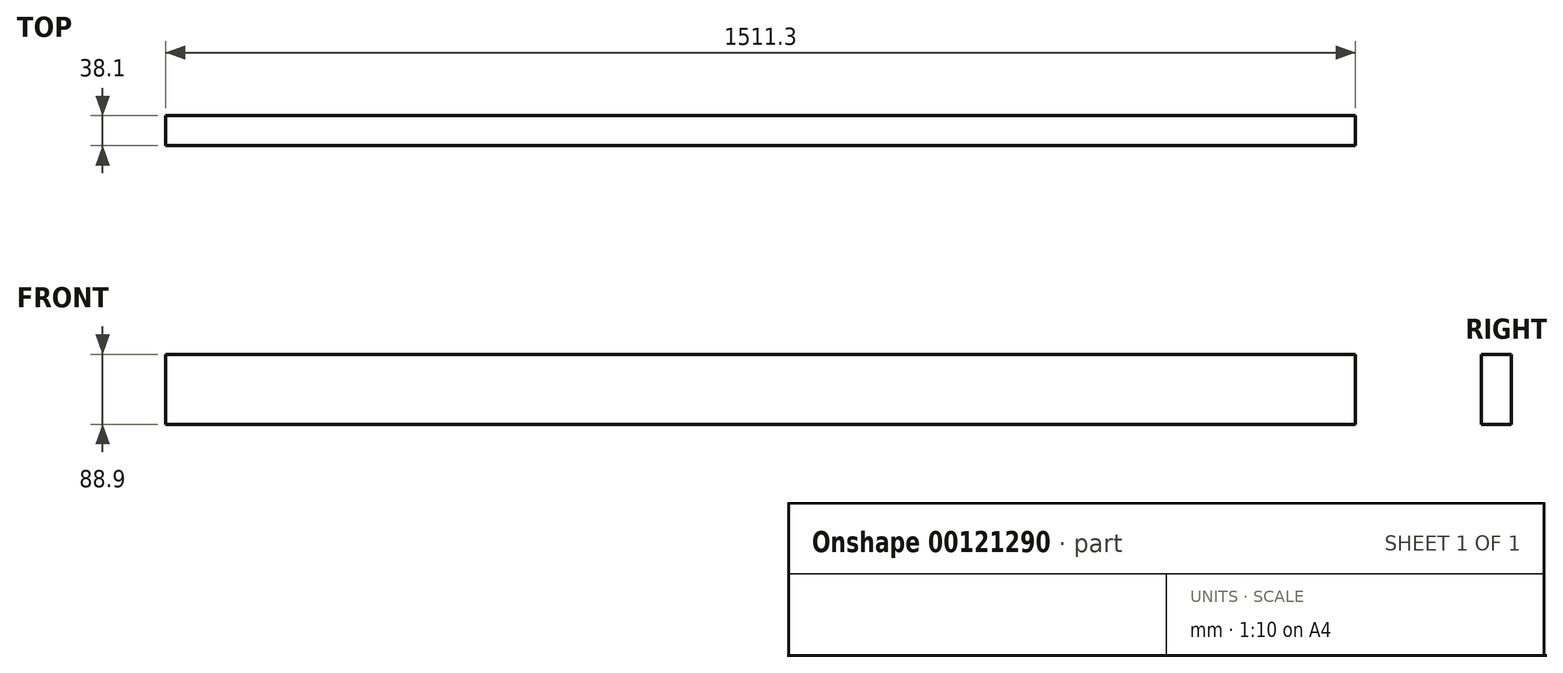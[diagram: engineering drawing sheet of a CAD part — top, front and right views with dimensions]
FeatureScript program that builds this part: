
annotation { "Feature Type Name" : "Feature", "Feature Type Description" : "" }
export const myFeature = defineFeature(function(context is Context, id is Id, definition is map)
    precondition{}
    {
        {
            var Q0;
            Q0=qCreatedBy(makeId("Front.planeOp"),FACE);
            var sketch = newSketch(context, id + "F0", { "sketchPlane" : qUnion([Q0])});
            skLineSegment(sketch, "E0.bottom", {"start": v(0, 0) * mm, "end": v(1511.3, 0) * mm});
            skLineSegment(sketch, "E0.top", {"start": v(0, 88.9) * mm, "end": v(1511.3, 88.9) * mm});
            skLineSegment(sketch, "E0.left", {"start": v(0, 0) * mm, "end": v(0, 88.9) * mm});
            skLineSegment(sketch, "E0.right", {"start": v(1511.3, 0) * mm, "end": v(1511.3, 88.9) * mm});
            skSolve(sketch);
        }
        {
            var Q0;
            Q0=makeQuery(id+"F0.imprint","IMPRINT",FACE,{"disambiguationData":[TD([[makeQuery(id+"F0.imprint","IMPRINT",EDGE,{"derivedFrom":sQuery(id+"F0.wireOp",EDGE,"E0.bottom")}),1.0]])]});
            extrude(context, id + "F1", {"entities" : qUnion([Q0]), "depth" : 38.1 * mm});
        }
    });
